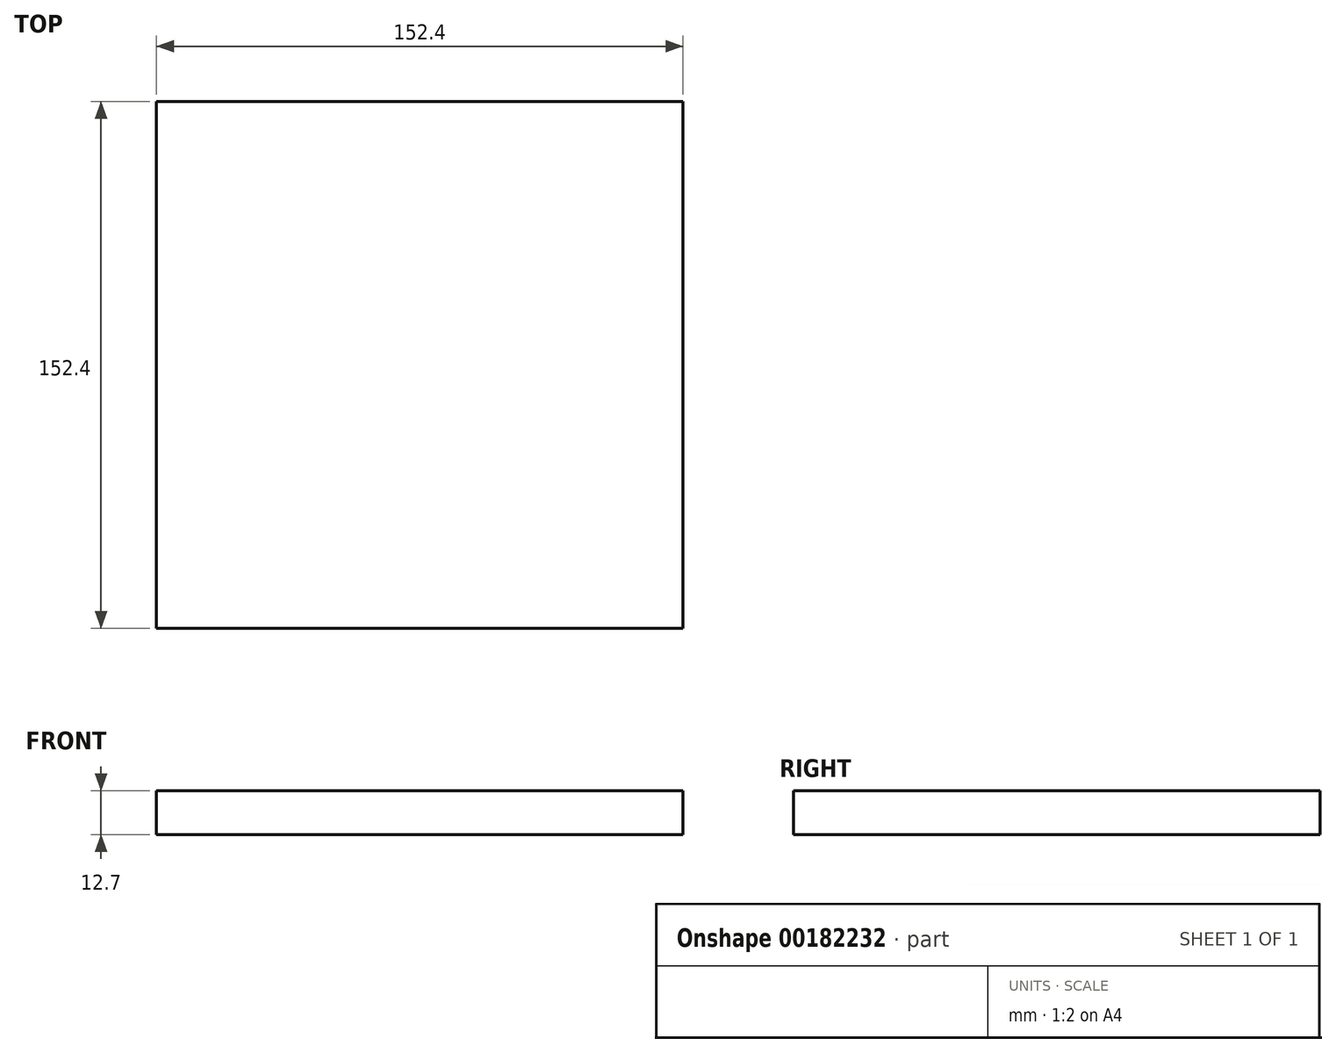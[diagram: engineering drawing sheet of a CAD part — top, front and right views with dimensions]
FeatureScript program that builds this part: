
annotation { "Feature Type Name" : "Feature", "Feature Type Description" : "" }
export const myFeature = defineFeature(function(context is Context, id is Id, definition is map)
    precondition{}
    {
        {
            var Q0;
            Q0=qCreatedBy(makeId("Top.planeOp"),FACE);
            var sketch = newSketch(context, id + "F0", { "sketchPlane" : qUnion([Q0])});
            skLineSegment(sketch, "E0.bottom", {"start": v(0, 0) * mm, "end": v(152.4, 0) * mm});
            skLineSegment(sketch, "E0.top", {"start": v(0, 152.4) * mm, "end": v(152.4, 152.4) * mm});
            skLineSegment(sketch, "E0.left", {"start": v(0, 0) * mm, "end": v(0, 152.4) * mm});
            skLineSegment(sketch, "E0.right", {"start": v(152.4, 0) * mm, "end": v(152.4, 152.4) * mm});
            skSolve(sketch);
        }
        {
            var Q0;
            Q0=makeQuery(id+"F0.imprint","IMPRINT",FACE,{"disambiguationData":[TD([[makeQuery(id+"F0.imprint","IMPRINT",EDGE,{"derivedFrom":sQuery(id+"F0.wireOp",EDGE,"E0.bottom")}),1.0]])]});
            extrude(context, id + "F1", {"entities" : qUnion([Q0]), "oppositeDirection" : true, "depth" : 12.7 * mm});
        }
    });
